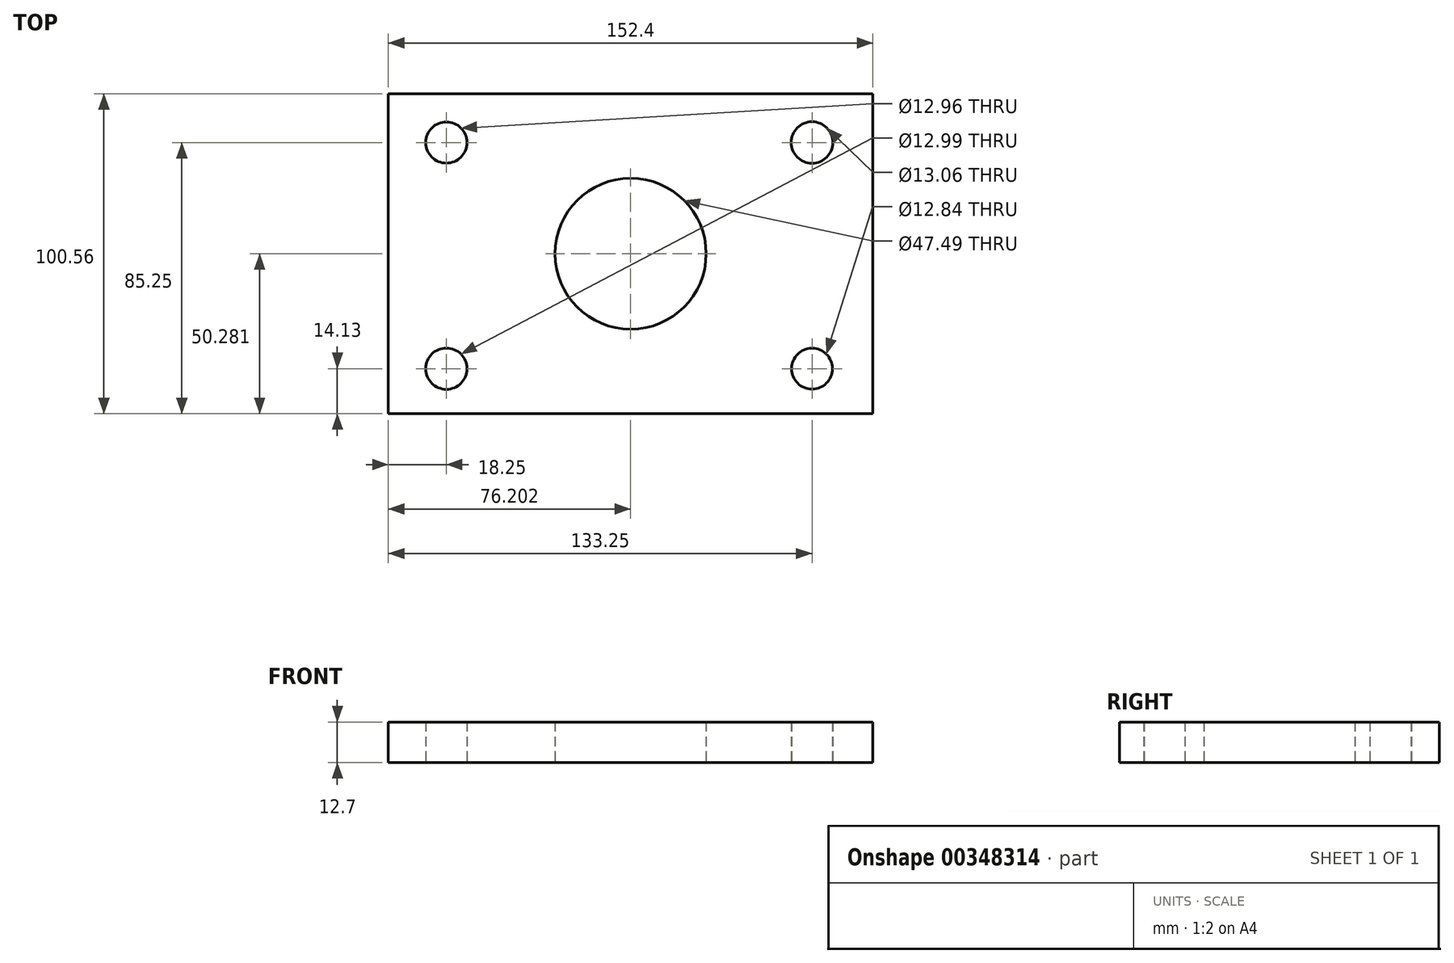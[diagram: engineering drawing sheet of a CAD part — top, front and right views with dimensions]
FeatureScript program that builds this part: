
annotation { "Feature Type Name" : "Feature", "Feature Type Description" : "" }
export const myFeature = defineFeature(function(context is Context, id is Id, definition is map)
    precondition{}
    {
        {
            var Q0;
            Q0=qCreatedBy(makeId("Top.planeOp"),FACE);
            var sketch = newSketch(context, id + "F0", { "sketchPlane" : qUnion([Q0])});
            skLineSegment(sketch, "E0.bottom", {"start": v(-75.75, 50.87) * mm, "end": v(76.65, 50.87) * mm});
            skLineSegment(sketch, "E0.top", {"start": v(-75.75, -49.69) * mm, "end": v(76.65, -49.69) * mm});
            skLineSegment(sketch, "E0.left", {"start": v(-75.75, 50.87) * mm, "end": v(-75.75, -49.69) * mm});
            skLineSegment(sketch, "E0.right", {"start": v(76.65, 50.87) * mm, "end": v(76.65, -49.69) * mm});
            skPoint(sketch, "E0.middle", {"position": v(0.45, 0.6) * mm});
            skLineSegment(sketch, "E1.bottom", {"start": v(-57.5, 35.56) * mm, "end": v(57.5, 35.56) * mm});
            skLineSegment(sketch, "E1.top", {"start": v(-57.5, -35.56) * mm, "end": v(57.5, -35.56) * mm});
            skLineSegment(sketch, "E1.left", {"start": v(-57.5, 35.56) * mm, "end": v(-57.5, -35.56) * mm});
            skLineSegment(sketch, "E1.right", {"start": v(57.5, 35.56) * mm, "end": v(57.5, -35.56) * mm});
            skPoint(sketch, "E1.middle", {"position": v(0, 0) * mm});
            skCircle(sketch, "E2", {"center": v(-57.5, 35.56) * mm, "radius": 6.48 * mm});
            skCircle(sketch, "E3", {"center": v(57.5, 35.56) * mm, "radius": 6.53 * mm});
            skCircle(sketch, "E4", {"center": v(57.5, -35.56) * mm, "radius": 6.42 * mm});
            skCircle(sketch, "E5", {"center": v(-57.5, -35.56) * mm, "radius": 6.5 * mm});
            skCircle(sketch, "E6", {"center": v(0.45, 0.6) * mm, "radius": 23.75 * mm});
            skSolve(sketch);
        }
        {
            var Q0;
            Q0=makeQuery(id+"F0.imprint","IMPRINT",FACE,{"disambiguationData":[TD([[makeQuery(id+"F0.imprint","IMPRINT",EDGE,{"derivedFrom":sQuery(id+"F0.wireOp",EDGE,"E0.bottom")}),-1.0]])]});
            var Q1;
            Q1=makeQuery(id+"F0.imprint","IMPRINT",FACE,{"disambiguationData":[TD([[makeQuery(id+"F0.imprint","IMPRINT",EDGE,{"derivedFrom":sQuery(id+"F0.wireOp",EDGE,"E6")}),-1.0]])]});
            extrude(context, id + "F1", {"entities" : qUnion([Q0, Q1]), "depth" : 12.7 * mm});
        }
    });
